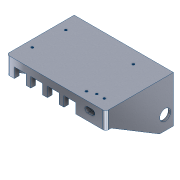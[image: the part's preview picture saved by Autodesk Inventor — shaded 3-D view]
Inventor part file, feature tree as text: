
AUTODESK INVENTOR PART (.ipt)
format: ipt  version: 2020 (Build 240168000, 168)  size: 906,752 bytes
history: native  units: in
note: dims shown in document units (in); Inventor stores cm internally (conversion verified against a paired STEP export)
features: reference x31, sketch x16, other x13, extrude x12, projected_geometry x9, plane x5, chamfer x2, helix x2, thicken_offset x1, fillet x1, mirror x1
ambient origin geometry x8: Origin, YZ Plane, XZ Plane, XY Plane, X Axis, Y Axis, Z Axis, Center Point
bodies: Solid1 (feature_tree)
feature tree (93):
  plane  "Work Plane1"
  extrude  "Extrusion1"  Depth=3.0in TaperAngle=0.0deg
  extrude  "Extrusion2"  Depth=0.25in
  plane  "Work Plane2"
  extrude  "Extrusion3"  Depth=0.005in
  thicken_offset  "Thicken1"
  extrude  "Extrusion4"  Depth=0.005in
  sketch  "Sketch5"  dims[d14=0.1795in d15=0.0in d16=0.105in]
  plane  "Work Plane3"
  extrude  "Extrusion5"  Depth=0.2in
  extrude  "Extrusion6"  Depth=0.105in
  extrude  "Extrusion7"  Depth=0.105in
  extrude  "Extrusion8"  Depth=0.089in
  extrude  "Extrusion9"  Depth=0.05in TaperAngle=45.0deg
  fillet  "Fillet1"  Radius=1.0in
  extrude  "Extrusion10"  Depth=1.0in TaperAngle=0.0deg
  mirror  "Mirror1"
  chamfer  "Chamfer1"  Distance=1.0in
  chamfer  "Chamfer2"  Distance=0.25in
  sketch  "Sketch11"  dims[d34=0.45in]
  plane  "Work Plane4"
  extrude  "Extrusion11"  Depth=0.325in
  helix  "Coil1"  [1 undecoded]
  sketch  "Sketch Driven Pattern1"  dims[d0=0.089in d1=3.0in d2=0.0in]
  sketch  "Sketch13"  dims[d38=0.089in d40=0.25in d41=0.0in]
  plane  "Work Plane5"
  helix  "Coil2"  [1 undecoded]
  sketch  "Sketch Driven Pattern2"  dims[d5=0.0in d6=0.0in d7=0.005in]
  extrude  "Extrusion12"  Depth=0.25in
  sketch  "Sketch1"  dims[d3=0.25in d4=0.625in]
  reference  "Reference1"
  reference  "Reference2"
  reference  "Reference3"
  reference  "Reference4"
  reference  "Reference5"
  reference  "Reference6"
  reference  "Reference7"
  reference  "Reference8"
  reference  "Reference9"
  reference  "Reference10"
  reference  "Reference11"
  reference  "Reference12"
  reference  "Reference13"
  reference  "Reference14"
  sketch  "Sketch2"  dims[d8=0.3125in d9=0.0in d10=0.005in]
  reference  "Reference15"
  reference  "Reference16"
  reference  "Reference17"
  reference  "Reference18"
  sketch  "Sketch4"  dims[d11=0.005in d13=0.2in]
  reference  "Reference23"
  reference  "Reference24"
  reference  "Reference25"
  reference  "Reference26"
  reference  "Reference27"
  reference  "Reference28"
  sketch  "Sketch6"  dims[d17=0.105in d18=0.105in]
  reference  "Reference29"
  sketch  "Sketch7"  dims[d19=0.3in d20=0.089in]
  sketch  "Sketch8"  dims[d21=1.0in d22=0.0in d23=0.05in d24=0.125in d25=45.0deg]
  reference  "Reference30"
  reference  "Reference31"
  sketch  "Sketch9"  dims[d26=0.0125in d27=0.125in d28=45.0deg d29=1.0in d30=0.0in]
  reference  "Reference32"
  reference  "Reference33"
  sketch  "Sketch10"  dims[d31=0.0197in d32=1.0in d33=0.0in]
  projected_geometry  "Projected Loop1"
  sketch  "Sketch12"  dims[d35=0.47in d36=1.0in d37=0.0in]
  projected_geometry  "Projected Loop2"
  projected_geometry  "Projected Loop3"
  projected_geometry  "Projected Loop4"
  projected_geometry  "Projected Loop5"
  projected_geometry  "Projected Loop6"
  projected_geometry  "Projected Loop7"
  projected_geometry  "Projected Loop8"
  reference  "Reference34"
  reference  "Reference35"
  sketch  "Sketch14"  dims[d42=0.125in d43=0.325in d44=0.1in d45=0.125in]
  projected_geometry  "Projected Loop9"
  sketch  "Sketch15"  dims[d46=0.125in d47=0.125in d48=0.125in d49=0.05in d50=0.0in d51=0.0in d52=0.0in d53=60.0deg d54=0.0188in d55=0.0063in d56=0.2487in d57=0.025in d58=0.2487in d59=0.3937in d60=0.0in d61=90.0deg d62=90.0deg d63=0.0in d64=0.0in d65=60.0deg d66=0.0188in d67=0.0063in d68=0.2687in d69=0.025in d70=0.2687in d71=0.3937in d72=0.0in d73=90.0deg d74=90.0deg d75=0.0in d76=0.0in d77=0.5in d78=0.375in d79=0.625in d80=1.0in d81=0.0in d82=0.25in]
  other  "<userpath>\Google Drive\Pirani Gauge\Pirani Gauge Modeling\Data Acquisition\Readout.iam"
  other  "Readout.iam"
  other  "Faceplate:1"
  other  "Gauge Controller:1"
  other  "RJ12 - 90deg:2"
  other  "RJ12 - 90deg:1"
  other  "RJ12 - 90deg:3"
  other  "RJ12 - 90deg:4"
  other  "PCB:1"
  other  "MicroUSB Breakout:1"
  other  "pcb_microusb:1"
  other  "Arduino Nano - Soldered:1"
  other  "USB-Mini-B:1"
note: 2 required parameter values undecoded (feature->parameter linkage not recoverable at this tier; creation-order binding heuristic only, values carry confidence <= 0.55)
